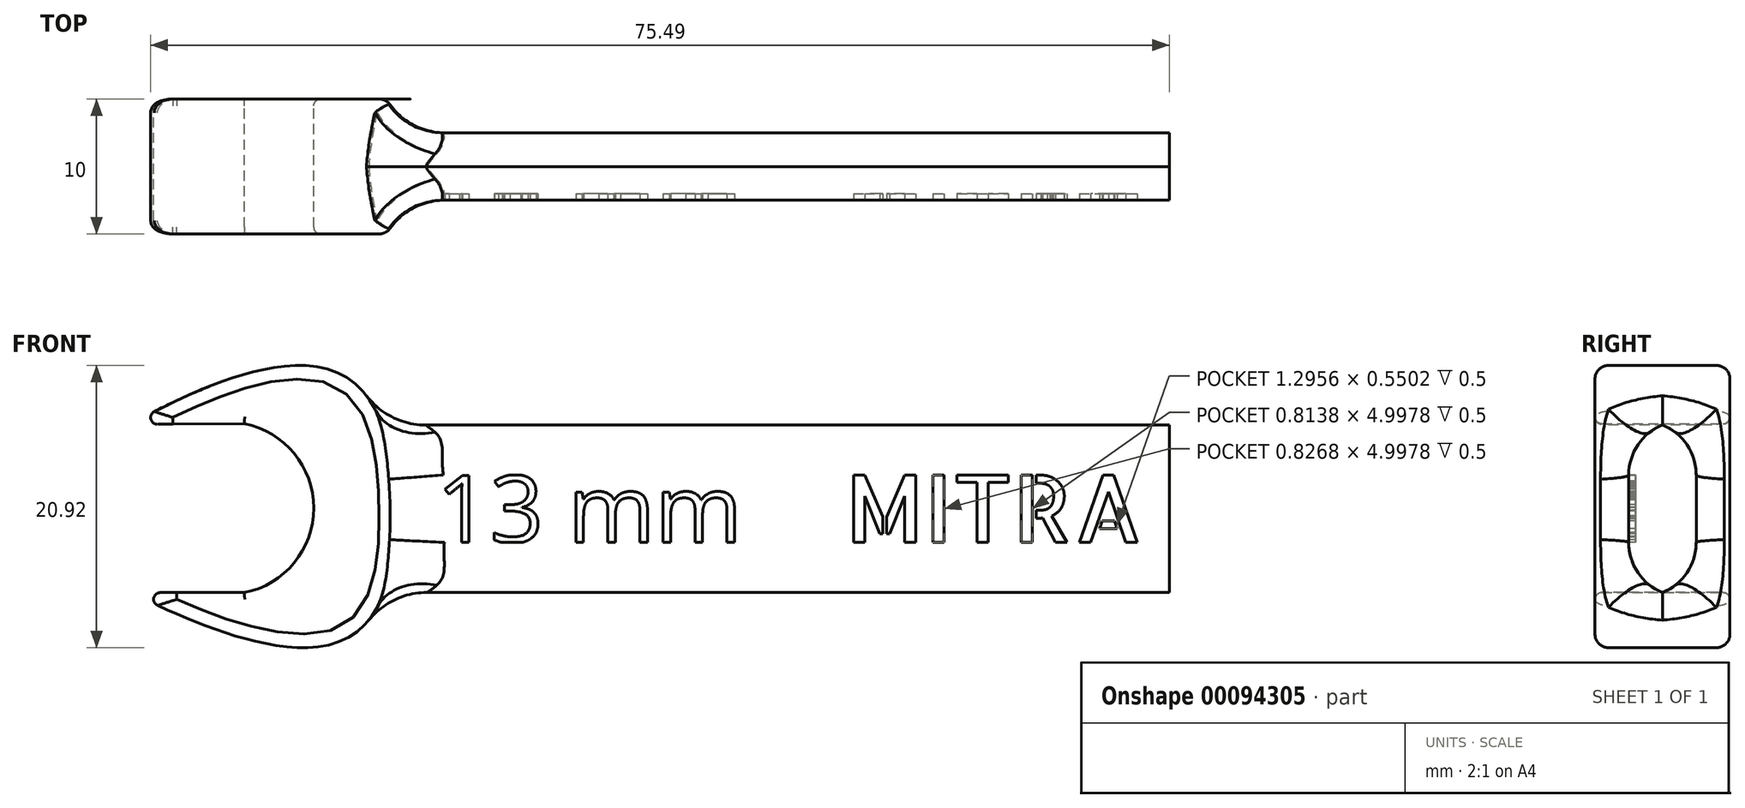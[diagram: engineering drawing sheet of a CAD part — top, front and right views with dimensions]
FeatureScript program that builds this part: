
annotation { "Feature Type Name" : "Feature", "Feature Type Description" : "" }
export const myFeature = defineFeature(function(context is Context, id is Id, definition is map)
    precondition{}
    {
        {
            var Q0;
            Q0=qCreatedBy(makeId("Front.planeOp"),FACE);
            var sketch = newSketch(context, id + "F0", { "sketchPlane" : qUnion([Q0])});
            skLineSegment(sketch, "E0.bottom", {"start": v(6.5, -6.5) * mm, "end": v(-6.5, -6.5) * mm});
            skLineSegment(sketch, "E0.top", {"start": v(6.5, 6.5) * mm, "end": v(-6.5, 6.5) * mm});
            skLineSegment(sketch, "E0.left", {"start": v(6.5, -6.5) * mm, "end": v(6.5, 6.5) * mm});
            skLineSegment(sketch, "E0.right", {"start": v(-6.5, -6.5) * mm, "end": v(-6.5, 6.5) * mm});
            skPoint(sketch, "E0.middle", {"position": v(0, 0) * mm});
            skSolve(sketch);
        }
        {
            var Q0;
            Q0=makeQuery(id+"F0.imprint","IMPRINT",FACE,{"disambiguationData":[TD([[makeQuery(id+"F0.imprint","IMPRINT",EDGE,{"derivedFrom":sQuery(id+"F0.wireOp",EDGE,"E0.bottom")}),-1.0]])]});
            var sketch = newSketch(context, id + "F1", { "sketchPlane" : qUnion([Q0])});
            skLineSegment(sketch, "E1", {"start": v(5, 0) * mm, "end": v(-8, 0) * mm});
            skLineSegment(sketch, "E2", {"start": v(0, -6.4) * mm, "end": v(-8.02, -6.4) * mm});
            skLineSegment(sketch, "E3", {"start": v(0, 6.51) * mm, "end": v(-8.02, 6.51) * mm});
            skSolve(sketch);
        }
        {
            var Q0;
            Q0=qCreatedBy(makeId("Front.planeOp"),FACE);
            var sketch = newSketch(context, id + "F2", { "sketchPlane" : qUnion([Q0])});
            skArc(sketch, "E4", {"start": v(0, -6.22) * mm, "mid": v(5.16, 0.04) * mm, "end": v(0, 6.3) * mm});
            skFitSpline(sketch, "E5", {"points": [v(-8.46, 6.24) * mm, v(11, 0) * mm, v(-8.4, -6.22) * mm], "startDerivative": vector(104.42, 57.64) * mm, "endDerivative": vector(-107.07, 53.6) * mm});
            skLineSegment(sketch, "E6", {"start": v(0, -6.22) * mm, "end": v(-8.4, -6.22) * mm});
            skLineSegment(sketch, "E7", {"start": v(0, 6.3) * mm, "end": v(-8.46, 6.24) * mm});
            skSolve(sketch);
        }
        {
            var Q0;
            Q0=qCreatedBy(makeId("Front.planeOp"),FACE);
            var sketch = newSketch(context, id + "F3", { "sketchPlane" : qUnion([Q0])});
            skLineSegment(sketch, "E8.bottom", {"start": v(5.56, -6.5) * mm, "end": v(68.56, -6.5) * mm});
            skLineSegment(sketch, "E8.top", {"start": v(5.56, 6.5) * mm, "end": v(68.56, 6.5) * mm});
            skLineSegment(sketch, "E8.left", {"start": v(5.56, -6.5) * mm, "end": v(5.56, 6.5) * mm});
            skLineSegment(sketch, "E8.right", {"start": v(68.56, -6.5) * mm, "end": v(68.56, 6.5) * mm});
            skPoint(sketch, "E8.middle", {"position": v(37.06, 0) * mm});
            skSolve(sketch);
        }
        {
            var Q0;
            Q0=makeQuery(id+"F2.imprint","IMPRINT",FACE,{"disambiguationData":[TD([[makeQuery(id+"F2.imprint","IMPRINT",EDGE,{"derivedFrom":sQuery(id+"F2.wireOp",EDGE,"E4")}),-1.0]])]});
            extrude(context, id + "F4", {"entities" : qUnion([Q0]), "endBound" : BoundingType.SYMMETRIC, "depth" : 10 * mm});
        }
        {
            var Q0;
            Q0=makeQuery(id+"F3.imprint","IMPRINT",FACE,{"disambiguationData":[TD([[makeQuery(id+"F3.imprint","IMPRINT",EDGE,{"derivedFrom":sQuery(id+"F3.wireOp",EDGE,"E8.bottom")}),1.0]])]});
            extrude(context, id + "F5", {"entities" : qUnion([Q0]), "operationType" : NewBodyOperationType.ADD, "endBound" : BoundingType.SYMMETRIC, "depth" : 5 * mm});
        }
        {
            var Q0;
            Q0=makeQuery(id+"F5.opExtrude","CAP_EDGE",EDGE,{"disambiguationData":[OSD([sQuery(id+"F3.wireOp",EDGE,"E8.top")])],"isStart":false});
            var Q1;
            Q1=makeQuery(id+"F5.opExtrude","CAP_EDGE",EDGE,{"disambiguationData":[OSD([sQuery(id+"F3.wireOp",EDGE,"E8.top")])],"isStart":true});
            fillet(context, id + "F6", {"entities" : qUnion([Q0, Q1]), "radius" : 4 * mm, "tangentPropagation" : true, "allowEdgeOverflow" : false});
        }
        {
            var Q0;
            Q0=makeQuery(id+"F5.opExtrude","CAP_EDGE",EDGE,{"disambiguationData":[OSD([sQuery(id+"F3.wireOp",EDGE,"E8.bottom")])],"isStart":false});
            var Q1;
            Q1=makeQuery(id+"F5.opExtrude","CAP_EDGE",EDGE,{"disambiguationData":[OSD([sQuery(id+"F3.wireOp",EDGE,"E8.bottom")])],"isStart":true});
            fillet(context, id + "F7", {"entities" : qUnion([Q0, Q1]), "radius" : 4 * mm, "tangentPropagation" : true, "allowEdgeOverflow" : false});
        }
        {
            var Q0;
            Q0=makeQuery(id+"F4.opExtrude","CAP_EDGE",EDGE,{"disambiguationData":[OSD([sQuery(id+"F2.wireOp",EDGE,"E5")])],"isStart":true});
            var Q1;
            Q1=makeQuery(id+"F4.opExtrude","CAP_EDGE",EDGE,{"disambiguationData":[OSD([sQuery(id+"F2.wireOp",EDGE,"E5")])],"isStart":false});
            fillet(context, id + "F8", {"entities" : qUnion([Q0, Q1]), "radius" : 1 * mm, "tangentPropagation" : true, "allowEdgeOverflow" : false});
        }
        {
            var Q0;
            Q0=makeQuery(id+"F4.opExtrude","CAP_EDGE",EDGE,{"disambiguationData":[OSD([sQuery(id+"F2.wireOp",EDGE,"E4")])],"isStart":false});
            var Q1;
            Q1=makeQuery(id+"F4.opExtrude","CAP_EDGE",EDGE,{"disambiguationData":[OSD([sQuery(id+"F2.wireOp",EDGE,"E4")])],"isStart":true});
            fillet(context, id + "F9", {"entities" : qUnion([Q0, Q1]), "radius" : .5 * mm, "tangentPropagation" : true, "allowEdgeOverflow" : false});
        }
        {
            var Q0;
            Q0=makeQuery(id+"F4.opExtrude","CAP_EDGE",EDGE,{"disambiguationData":[OSD([sQuery(id+"F2.wireOp",EDGE,"E7")])],"isStart":true});
            var Q1;
            Q1=makeQuery(id+"F4.opExtrude","CAP_EDGE",EDGE,{"disambiguationData":[OSD([sQuery(id+"F2.wireOp",EDGE,"E7")])],"isStart":false});
            var Q2;
            Q2=makeQuery(id+"F4.opExtrude","CAP_EDGE",EDGE,{"disambiguationData":[OSD([sQuery(id+"F2.wireOp",EDGE,"E6")])],"isStart":false});
            var Q3;
            Q3=makeQuery(id+"F4.opExtrude","CAP_EDGE",EDGE,{"disambiguationData":[OSD([sQuery(id+"F2.wireOp",EDGE,"E6")])],"isStart":true});
            fillet(context, id + "F10", {"entities" : qUnion([Q0, Q1, Q2, Q3]), "radius" : .5 * mm, "tangentPropagation" : true, "allowEdgeOverflow" : false});
        }
        {
            var Q0;
            Q0=makeQuery(id+"F5.opExtrude","CAP_FACE",FACE,{"disambiguationData":[OSD([sQuery(id+"F3.wireOp",EDGE,"E8.bottom"),sQuery(id+"F3.wireOp",EDGE,"E8.top"),sQuery(id+"F3.wireOp",EDGE,"E8.left"),sQuery(id+"F3.wireOp",EDGE,"E8.right")])],"isStart":false});
            var sketch = newSketch(context, id + "F11", { "sketchPlane" : qUnion([Q0])});
            skText(sketch, "E9", { "text": "13 mm", "fontName": "OpenSans-Regular.ttf"});
            const initialGuessF11  = {"E9": [0.01424, -0.0025, 1, 0, 0.005]};
            skSetInitialGuess(sketch, initialGuessF11);
            skSolve(sketch);
        }
        {
            var Q0;
            Q0=makeQuery(id+"F11.imprint","IMPRINT",FACE,{"disambiguationData":[TD([[makeQuery(id+"F11.imprint","IMPRINT",EDGE,{"derivedFrom":sQuery(id+"F11.wireOp",EDGE,"E9.sketch_text.stroke-9")}),-1.0]])]});
            var Q1;
            Q1=makeQuery(id+"F11.imprint","IMPRINT",FACE,{"disambiguationData":[TD([[makeQuery(id+"F11.imprint","IMPRINT",EDGE,{"derivedFrom":sQuery(id+"F11.wireOp",EDGE,"E9.sketch_text.stroke-37")}),-1.0]])]});
            var Q2;
            Q2=makeQuery(id+"F11.imprint","IMPRINT",FACE,{"disambiguationData":[TD([[makeQuery(id+"F11.imprint","IMPRINT",EDGE,{"derivedFrom":sQuery(id+"F11.wireOp",EDGE,"E9.sketch_text.stroke-65")}),-1.0]])]});
            var Q3;
            Q3=makeQuery(id+"F11.imprint","IMPRINT",FACE,{"disambiguationData":[TD([[makeQuery(id+"F11.imprint","IMPRINT",EDGE,{"derivedFrom":sQuery(id+"F11.wireOp",EDGE,"E9.sketch_text.stroke-0")}),1.0]])]});
            extrude(context, id + "F12", {"entities" : qUnion([Q0, Q1, Q2, Q3]), "operationType" : NewBodyOperationType.REMOVE, "oppositeDirection" : true, "depth" : .5 * mm});
        }
        {
            var Q0;
            Q0=makeQuery(id+"F6.opFillet","BLEND_EDGE",EDGE,{"blendedFrom":[makeQuery(id+"F5.opExtrude","CAP_EDGE",EDGE,{"disambiguationData":[OSD([sQuery(id+"F3.wireOp",EDGE,"E8.top")])],"isStart":true}),makeQuery(id+"F4.opExtrude","SWEPT_FACE",FACE,{"disambiguationData":[OSD([sQuery(id+"F2.wireOp",EDGE,"E5")])]})],"blendedInto":[makeQuery(id+"F4.opExtrude","SWEPT_FACE",FACE,{"disambiguationData":[OSD([sQuery(id+"F2.wireOp",EDGE,"E5")])]})]});
            var Q1;
            Q1=makeQuery(id+"F6.opFillet","BLEND_EDGE",EDGE,{"blendedFrom":[makeQuery(id+"F5.opExtrude","CAP_EDGE",EDGE,{"disambiguationData":[OSD([sQuery(id+"F3.wireOp",EDGE,"E8.top")])],"isStart":false}),makeQuery(id+"F4.opExtrude","SWEPT_FACE",FACE,{"disambiguationData":[OSD([sQuery(id+"F2.wireOp",EDGE,"E5")])]})],"blendedInto":[makeQuery(id+"F4.opExtrude","SWEPT_FACE",FACE,{"disambiguationData":[OSD([sQuery(id+"F2.wireOp",EDGE,"E5")])]})]});
            fillet(context, id + "F13", {"entities" : qUnion([Q0, Q1]), "radius" : 5 * mm, "tangentPropagation" : true, "allowEdgeOverflow" : false});
        }
        {
            var Q0;
            {var subQ1=sQuery(id+"F3.wireOp",EDGE,"E8.right");var subQ2=sQuery(id+"F3.wireOp",EDGE,"E8.left");var subQ3=sQuery(id+"F3.wireOp",EDGE,"E8.top");var subQ4=sQuery(id+"F3.wireOp",EDGE,"E8.bottom");var subQ5=makeQuery(id+"F5.opExtrude","CAP_FACE",FACE,{"disambiguationData":[OSD([subQ4,subQ3,subQ2,subQ1])],"isStart":false});var subQ6=subQ5;Q0=makeQuery(id+"F12.boolean.opBoolean","SPLIT",FACE,{"disambiguationData":[TD([makeQuery(id+"F5.opExtrude","SWEPT_FACE",FACE,{"disambiguationData":[OSD([subQ1])]})])],"derivedFrom":subQ6});}
            var sketch = newSketch(context, id + "F14", { "sketchPlane" : qUnion([Q0])});
            skText(sketch, "E10", { "text": "MITRA", "fontName": "AllertaStencil-Regular.ttf"});
            const initialGuessF14  = {"E10": [0.04453, -0.0025, 1, 0, 0.005]};
            skSetInitialGuess(sketch, initialGuessF14);
            skSolve(sketch);
        }
        {
            var Q0;
            Q0=makeQuery(id+"F14.imprint","IMPRINT",FACE,{"disambiguationData":[TD([[makeQuery(id+"F14.imprint","IMPRINT",EDGE,{"derivedFrom":sQuery(id+"F14.wireOp",EDGE,"E10.sketch_text.stroke-0")}),-1.0]])]});
            var Q1;
            Q1=makeQuery(id+"F14.imprint","IMPRINT",FACE,{"disambiguationData":[TD([[makeQuery(id+"F14.imprint","IMPRINT",EDGE,{"derivedFrom":sQuery(id+"F14.wireOp",EDGE,"E10.sketch_text.stroke-8")}),-1.0]])]});
            var Q2;
            Q2=makeQuery(id+"F14.imprint","IMPRINT",FACE,{"disambiguationData":[TD([[makeQuery(id+"F14.imprint","IMPRINT",EDGE,{"derivedFrom":sQuery(id+"F14.wireOp",EDGE,"E10.sketch_text.stroke-16")}),1.0]])]});
            var Q3;
            Q3=makeQuery(id+"F14.imprint","IMPRINT",FACE,{"disambiguationData":[TD([[makeQuery(id+"F14.imprint","IMPRINT",EDGE,{"derivedFrom":sQuery(id+"F14.wireOp",EDGE,"E10.sketch_text.stroke-20")}),-1.0]])]});
            var Q4;
            Q4=makeQuery(id+"F14.imprint","IMPRINT",FACE,{"disambiguationData":[TD([[makeQuery(id+"F14.imprint","IMPRINT",EDGE,{"derivedFrom":sQuery(id+"F14.wireOp",EDGE,"E10.sketch_text.stroke-28")}),-1.0]])]});
            var Q5;
            Q5=makeQuery(id+"F14.imprint","IMPRINT",FACE,{"disambiguationData":[TD([[makeQuery(id+"F14.imprint","IMPRINT",EDGE,{"derivedFrom":sQuery(id+"F14.wireOp",EDGE,"E10.sketch_text.stroke-32")}),1.0]])]});
            var Q6;
            Q6=makeQuery(id+"F14.imprint","IMPRINT",FACE,{"disambiguationData":[TD([[makeQuery(id+"F14.imprint","IMPRINT",EDGE,{"derivedFrom":sQuery(id+"F14.wireOp",EDGE,"E10.sketch_text.stroke-58")}),1.0]])]});
            var Q7;
            Q7=makeQuery(id+"F14.imprint","IMPRINT",FACE,{"disambiguationData":[TD([[makeQuery(id+"F14.imprint","IMPRINT",EDGE,{"derivedFrom":sQuery(id+"F14.wireOp",EDGE,"E10.sketch_text.stroke-65")}),-1.0]])]});
            extrude(context, id + "F15", {"entities" : qUnion([Q0, Q1, Q2, Q3, Q4, Q5, Q6, Q7]), "operationType" : NewBodyOperationType.REMOVE, "oppositeDirection" : true, "depth" : 0.5 * mm});
        }
    });
